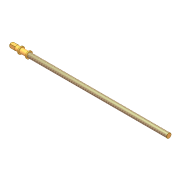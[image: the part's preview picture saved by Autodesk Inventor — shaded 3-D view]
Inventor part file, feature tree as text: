
AUTODESK INVENTOR PART (.ipt)
format: ipt  version: unknown  size: 199,168 bytes
history: native  units: in
note: dims shown in document units (in); Inventor stores cm internally (conversion verified against a paired STEP export)
features: chamfer x2, sketch x2, revolve x1, extrude x1, thread x1
ambient origin geometry x8: Origin, YZ Plane, XZ Plane, XY Plane, X Axis, Y Axis, Z Axis, Center Point
feature tree (7):
  revolve  "Revolution1"  [1 undecoded]
  chamfer  "Chamfer7"  Distance=0.1969in
  chamfer  "Chamfer8"  Distance=0.0787in
  extrude  "Extrusion19"  Depth=0.0787in
  thread  "Thread8"  [1 undecoded]
  sketch  "Sketch15"  dims[d21=0.7874in d84=0.1969in]
  sketch  "Sketch20"  dims[d92=90.0deg d127=0.1969in d128=0.0787in d129=0.0787in d130=0.5906in d135=0.0157in d136=0.0787in d137=45.0deg d144=0.0in d148=0.7874in d149=0.1969in d150=0.0394in d151=0.0787in d152=45.0deg d153=0.2835in d154=0.4724in d155=0.0in d156=11.811in d159=0.0787in d160=0.3937in d161=0.0in]
note: 2 required parameter values undecoded (feature->parameter linkage not recoverable at this tier; creation-order binding heuristic only, values carry confidence <= 0.55)